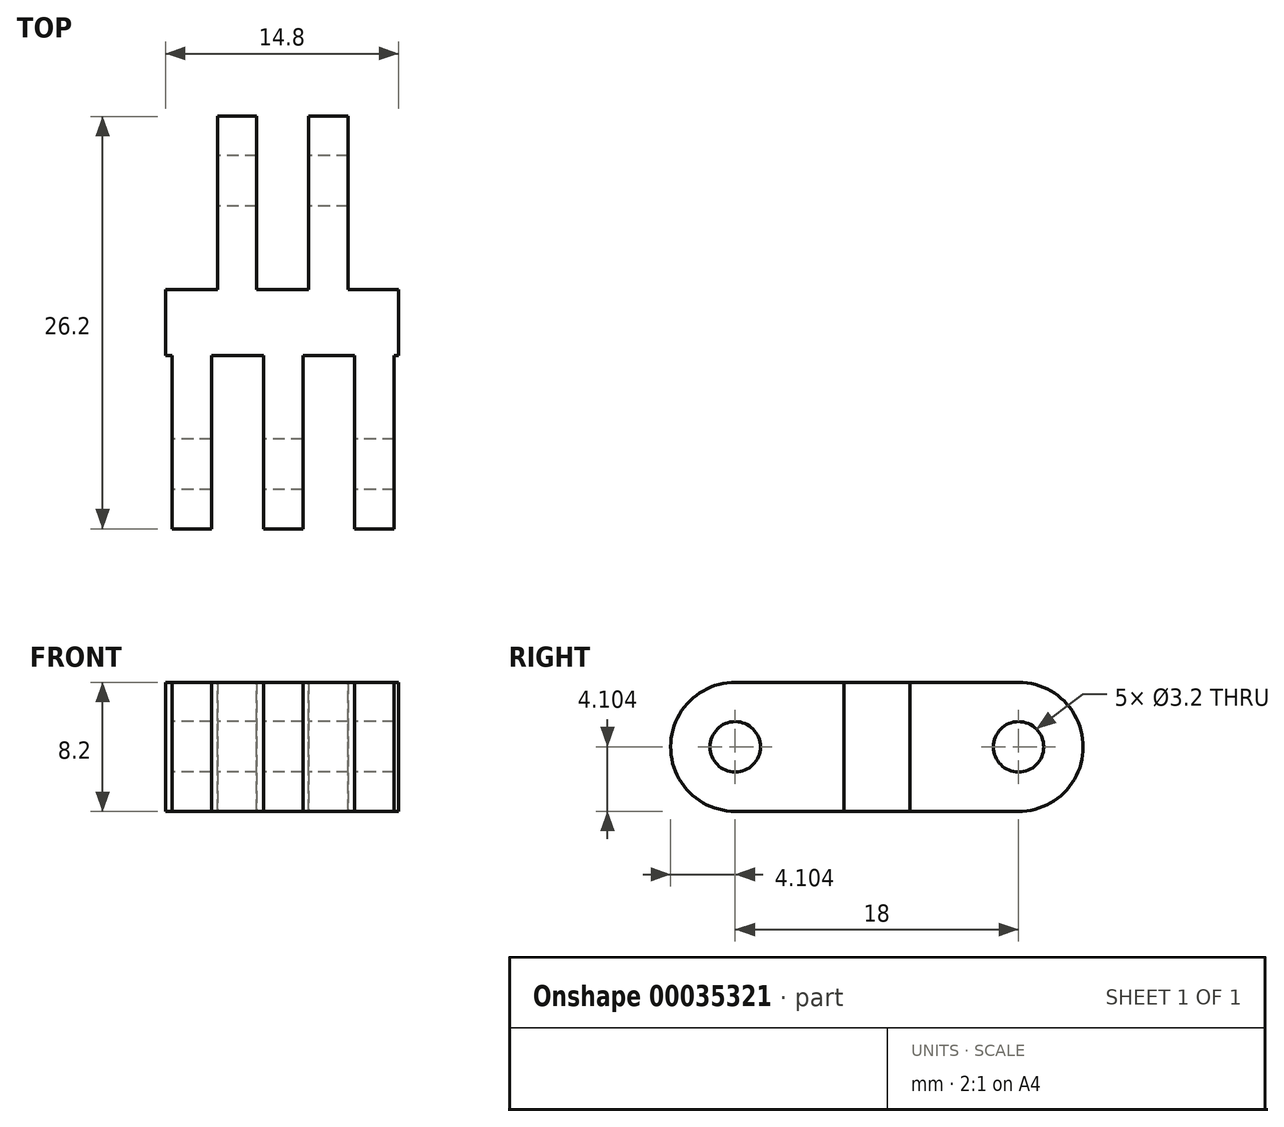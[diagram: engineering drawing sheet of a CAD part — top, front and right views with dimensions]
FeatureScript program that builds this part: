
annotation { "Feature Type Name" : "Feature", "Feature Type Description" : "" }
export const myFeature = defineFeature(function(context is Context, id is Id, definition is map)
    precondition{}
    {
        {
            var Q0;
            Q0=qCreatedBy(makeId("Right.planeOp"),FACE);
            var sketch = newSketch(context, id + "F0", { "sketchPlane" : qUnion([Q0])});
            skCircle(sketch, "E0", {"center": v(-26.56, 10.98) * mm, "radius": 1.6 * mm});
            skCircle(sketch, "E1", {"center": v(-26.56, 10.98) * mm, "radius": 4.1 * mm});
            skCircle(sketch, "E2", {"center": v(-8.56, 10.98) * mm, "radius": 1.6 * mm});
            skCircle(sketch, "E3", {"center": v(-8.56, 10.98) * mm, "radius": 4.1 * mm});
            skLineSegment(sketch, "E4", {"start": v(-26.59, 15.08) * mm, "end": v(-8.56, 15.08) * mm});
            skLineSegment(sketch, "E5", {"start": v(-8.53, 6.88) * mm, "end": v(-26.56, 6.88) * mm});
            skPoint(sketch, "E6", {"position": v(-4.46, 10.98) * mm});
            skPoint(sketch, "E7", {"position": v(-30.66, 10.98) * mm});
            skSolve(sketch);
        }
        {
            var Q0;
            Q0 = qSketchRegion(id + "F0", true);
            extrude(context, id + "F1", {"entities" : qUnion([Q0]), "depth" : 14.8 * mm});
        }
        {
            var Q0;
            Q0=qCreatedBy(makeId("Top.planeOp"),FACE);
            var sketch = newSketch(context, id + "F2", { "sketchPlane" : qUnion([Q0])});
            skLineSegment(sketch, "E8.bottom", {"start": v(0, -4.46) * mm, "end": v(3.3, -4.46) * mm});
            skLineSegment(sketch, "E8.top", {"start": v(0, -15.46) * mm, "end": v(3.3, -15.46) * mm});
            skLineSegment(sketch, "E8.left", {"start": v(0, -4.46) * mm, "end": v(0, -15.46) * mm});
            skLineSegment(sketch, "E8.right", {"start": v(3.3, -4.46) * mm, "end": v(3.3, -15.46) * mm});
            skLineSegment(sketch, "E9.1.0.0", {"start": v(5.8, -4.46) * mm, "end": v(9.1, -4.46) * mm});
            skLineSegment(sketch, "E9.1.0.1", {"start": v(5.8, -15.46) * mm, "end": v(9.1, -15.46) * mm});
            skLineSegment(sketch, "E9.1.0.2", {"start": v(5.8, -4.46) * mm, "end": v(5.8, -15.46) * mm});
            skLineSegment(sketch, "E9.1.0.3", {"start": v(9.1, -4.46) * mm, "end": v(9.1, -15.46) * mm});
            skLineSegment(sketch, "E9.2.0.0", {"start": v(11.6, -4.46) * mm, "end": v(14.9, -4.46) * mm});
            skLineSegment(sketch, "E9.2.0.1", {"start": v(11.6, -15.46) * mm, "end": v(14.9, -15.46) * mm});
            skLineSegment(sketch, "E9.2.0.2", {"start": v(11.6, -4.46) * mm, "end": v(11.6, -15.46) * mm});
            skLineSegment(sketch, "E9.2.0.3", {"start": v(14.9, -4.46) * mm, "end": v(14.9, -15.46) * mm});
            skLineSegment(sketch, "E9.direction1", {"start": v(0, -4.46) * mm, "end": v(5.8, -4.46) * mm, "construction": true});
            skSolve(sketch);
        }
        {
            var Q0;
            Q0 = qSketchRegion(id + "F2", true);
            extrude(context, id + "F3", {"entities" : qUnion([Q0]), "depth" : 24.7 * mm});
        }
        {
            var Q0;
            Q0=makeQuery(id+"F3.opExtrude","SWEPT_BODY",BODY,{"disambiguationData":[OSD([sQuery(id+"F2.wireOp",EDGE,"E8.bottom"),sQuery(id+"F2.wireOp",EDGE,"E8.top"),sQuery(id+"F2.wireOp",EDGE,"E8.left"),sQuery(id+"F2.wireOp",EDGE,"E8.right")])]});
            var Q1;
            Q1=makeQuery(id+"F3.opExtrude","SWEPT_BODY",BODY,{"disambiguationData":[OSD([sQuery(id+"F2.wireOp",EDGE,"E9.1.0.0"),sQuery(id+"F2.wireOp",EDGE,"E9.1.0.1"),sQuery(id+"F2.wireOp",EDGE,"E9.1.0.2"),sQuery(id+"F2.wireOp",EDGE,"E9.1.0.3")])]});
            var Q2;
            Q2=makeQuery(id+"F3.opExtrude","SWEPT_BODY",BODY,{"disambiguationData":[OSD([sQuery(id+"F2.wireOp",EDGE,"E9.2.0.0"),sQuery(id+"F2.wireOp",EDGE,"E9.2.0.1"),sQuery(id+"F2.wireOp",EDGE,"E9.2.0.2"),sQuery(id+"F2.wireOp",EDGE,"E9.2.0.3")])]});
            var Q3;
            Q3=makeQuery(id+"F1.opExtrude","SWEPT_BODY",BODY,{"disambiguationData":[OSD([sQuery(id+"F0.wireOp",EDGE,"E0"),sQuery(id+"F0.wireOp",EDGE,"E1"),sQuery(id+"F0.wireOp",EDGE,"E2"),sQuery(id+"F0.wireOp",EDGE,"E3"),sQuery(id+"F0.wireOp",EDGE,"E4"),sQuery(id+"F0.wireOp",EDGE,"E5")])]});
            booleanBodies(context, id + "F4", {"operationType" : BooleanOperationType.SUBTRACTION, "tools" : qUnion([Q0, Q1, Q2]), "targets" : qUnion([Q3])});
        }
        {
            var Q0;
            Q0=qCreatedBy(makeId("Top.planeOp"),FACE);
            var sketch = newSketch(context, id + "F5", { "sketchPlane" : qUnion([Q0])});
            skLineSegment(sketch, "E10.bottom", {"start": v(-2.88, -19.66) * mm, "end": v(0.42, -19.66) * mm});
            skLineSegment(sketch, "E10.top", {"start": v(-2.88, -30.66) * mm, "end": v(0.42, -30.66) * mm});
            skLineSegment(sketch, "E10.left", {"start": v(-2.88, -19.66) * mm, "end": v(-2.88, -30.66) * mm});
            skLineSegment(sketch, "E10.right", {"start": v(0.42, -19.66) * mm, "end": v(0.42, -30.66) * mm});
            skLineSegment(sketch, "E11.1.0.0", {"start": v(2.92, -19.66) * mm, "end": v(6.22, -19.66) * mm});
            skLineSegment(sketch, "E11.1.0.1", {"start": v(2.92, -30.66) * mm, "end": v(6.22, -30.66) * mm});
            skLineSegment(sketch, "E11.1.0.2", {"start": v(2.92, -19.66) * mm, "end": v(2.92, -30.66) * mm});
            skLineSegment(sketch, "E11.1.0.3", {"start": v(6.22, -19.66) * mm, "end": v(6.22, -30.66) * mm});
            skLineSegment(sketch, "E11.2.0.0", {"start": v(8.72, -19.66) * mm, "end": v(12.02, -19.66) * mm});
            skLineSegment(sketch, "E11.2.0.1", {"start": v(8.72, -30.66) * mm, "end": v(12.02, -30.66) * mm});
            skLineSegment(sketch, "E11.2.0.2", {"start": v(8.72, -19.66) * mm, "end": v(8.72, -30.66) * mm});
            skLineSegment(sketch, "E11.2.0.3", {"start": v(12.02, -19.66) * mm, "end": v(12.02, -30.66) * mm});
            skLineSegment(sketch, "E11.direction1", {"start": v(-2.88, -19.66) * mm, "end": v(2.92, -19.66) * mm, "construction": true});
            skLineSegment(sketch, "E12.0.3.0", {"start": v(14.52, -19.66) * mm, "end": v(17.82, -19.66) * mm});
            skLineSegment(sketch, "E12.3.3.0", {"start": v(14.52, -30.66) * mm, "end": v(17.82, -30.66) * mm});
            skLineSegment(sketch, "E12.6.3.0", {"start": v(14.52, -19.66) * mm, "end": v(14.52, -30.66) * mm});
            skLineSegment(sketch, "E12.9.3.0", {"start": v(17.82, -19.66) * mm, "end": v(17.82, -30.66) * mm});
            skSolve(sketch);
        }
        {
            var Q0;
            Q0 = qSketchRegion(id + "F5", true);
            extrude(context, id + "F6", {"entities" : qUnion([Q0]), "depth" : 25 * mm});
        }
        {
            var Q0;
            Q0=makeQuery(id+"F6.opExtrude","SWEPT_BODY",BODY,{"disambiguationData":[OSD([sQuery(id+"F5.wireOp",EDGE,"E10.bottom"),sQuery(id+"F5.wireOp",EDGE,"E10.top"),sQuery(id+"F5.wireOp",EDGE,"E10.left"),sQuery(id+"F5.wireOp",EDGE,"E10.right")])]});
            var Q1;
            Q1=makeQuery(id+"F6.opExtrude","SWEPT_BODY",BODY,{"disambiguationData":[OSD([sQuery(id+"F5.wireOp",EDGE,"E11.1.0.0"),sQuery(id+"F5.wireOp",EDGE,"E11.1.0.1"),sQuery(id+"F5.wireOp",EDGE,"E11.1.0.2"),sQuery(id+"F5.wireOp",EDGE,"E11.1.0.3")])]});
            var Q2;
            Q2=makeQuery(id+"F6.opExtrude","SWEPT_BODY",BODY,{"disambiguationData":[OSD([sQuery(id+"F5.wireOp",EDGE,"E11.2.0.0"),sQuery(id+"F5.wireOp",EDGE,"E11.2.0.1"),sQuery(id+"F5.wireOp",EDGE,"E11.2.0.2"),sQuery(id+"F5.wireOp",EDGE,"E11.2.0.3")])]});
            var Q3;
            Q3=makeQuery(id+"F6.opExtrude","SWEPT_BODY",BODY,{"disambiguationData":[OSD([sQuery(id+"F5.wireOp",EDGE,"E12.0.3.0"),sQuery(id+"F5.wireOp",EDGE,"E12.3.3.0"),sQuery(id+"F5.wireOp",EDGE,"E12.6.3.0"),sQuery(id+"F5.wireOp",EDGE,"E12.9.3.0")])]});
            var Q4;
            Q4=makeQuery(id+"F1.opExtrude","SWEPT_BODY",BODY,{"disambiguationData":[OSD([sQuery(id+"F0.wireOp",EDGE,"E0"),sQuery(id+"F0.wireOp",EDGE,"E1"),sQuery(id+"F0.wireOp",EDGE,"E2"),sQuery(id+"F0.wireOp",EDGE,"E3"),sQuery(id+"F0.wireOp",EDGE,"E4"),sQuery(id+"F0.wireOp",EDGE,"E5")])]});
            booleanBodies(context, id + "F7", {"operationType" : BooleanOperationType.SUBTRACTION, "tools" : qUnion([Q0, Q1, Q2, Q3]), "targets" : qUnion([Q4])});
        }
    });
